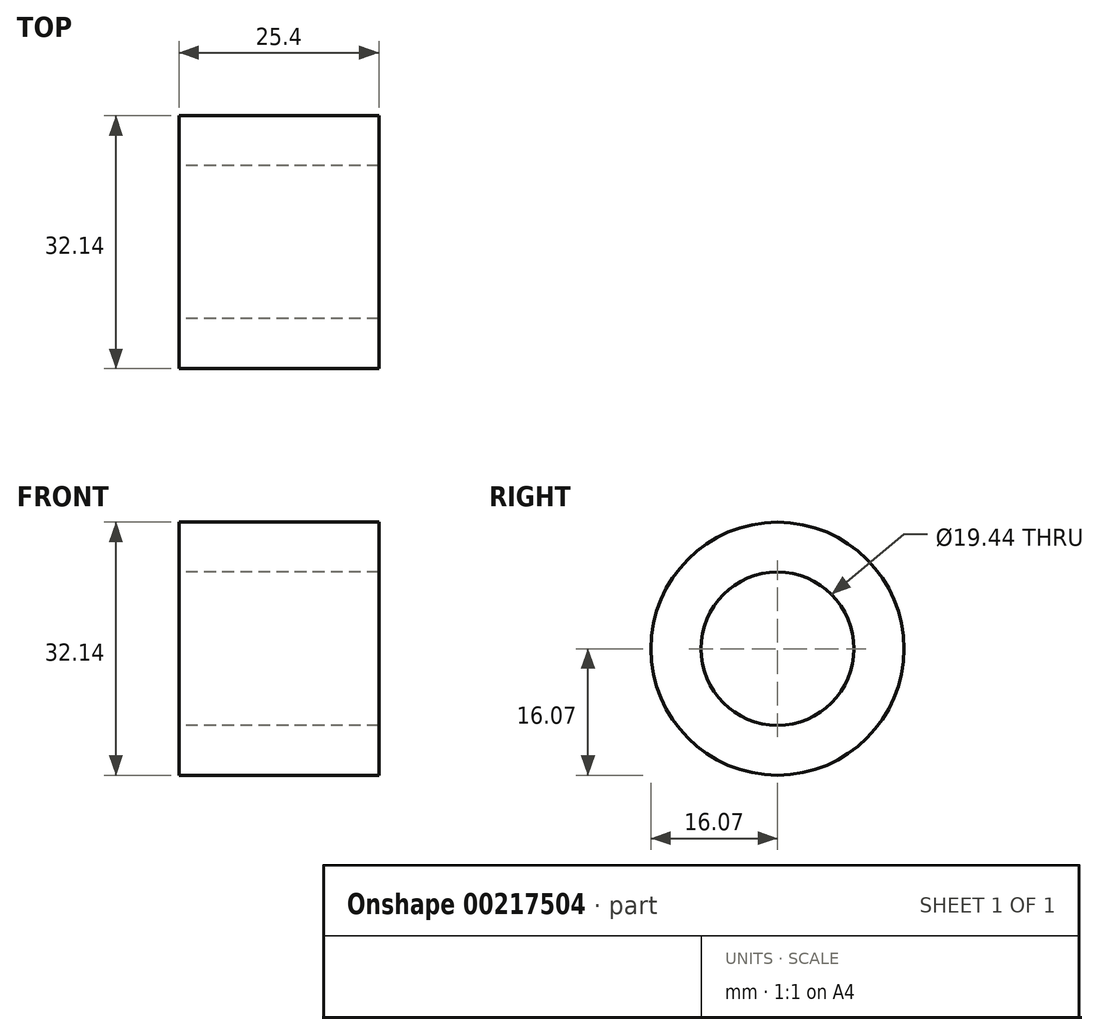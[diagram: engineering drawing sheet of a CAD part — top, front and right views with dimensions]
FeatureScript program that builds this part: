
annotation { "Feature Type Name" : "Feature", "Feature Type Description" : "" }
export const myFeature = defineFeature(function(context is Context, id is Id, definition is map)
    precondition{}
    {
        {
            var Q0;
            Q0=qCreatedBy(makeId("Right.planeOp"),FACE);
            var sketch = newSketch(context, id + "F0", { "sketchPlane" : qUnion([Q0])});
            skCircle(sketch, "E0", {"center": v(0, 0) * mm, "radius": 9.72 * mm});
            skSolve(sketch);
        }
        {
            var Q0;
            Q0=qCreatedBy(makeId("Right.planeOp"),FACE);
            var sketch = newSketch(context, id + "F1", { "sketchPlane" : qUnion([Q0])});
            skCircle(sketch, "E1.0", {"center": v(0, 0) * mm, "radius": 16.07 * mm});
            skSolve(sketch);
        }
        {
            var Q0;
            Q0=makeQuery(id+"F1.imprint","IMPRINT",FACE,{"disambiguationData":[TD([[makeQuery(id+"F1.imprint","IMPRINT",EDGE,{"derivedFrom":sQuery(id+"F1.wireOp",EDGE,"E1.0")}),1.0]])]});
            extrude(context, id + "F2", {"entities" : qUnion([Q0]), "depth" : 25.4 * mm});
        }
        {
            var Q0;
            Q0=makeQuery(id+"F0.imprint","IMPRINT",FACE,{"disambiguationData":[TD([[makeQuery(id+"F0.imprint","IMPRINT",EDGE,{"derivedFrom":sQuery(id+"F0.wireOp",EDGE,"E0")}),1.0]])]});
            extrude(context, id + "F3", {"entities" : qUnion([Q0]), "operationType" : NewBodyOperationType.REMOVE, "depth" : 25.4 * mm});
        }
    });
